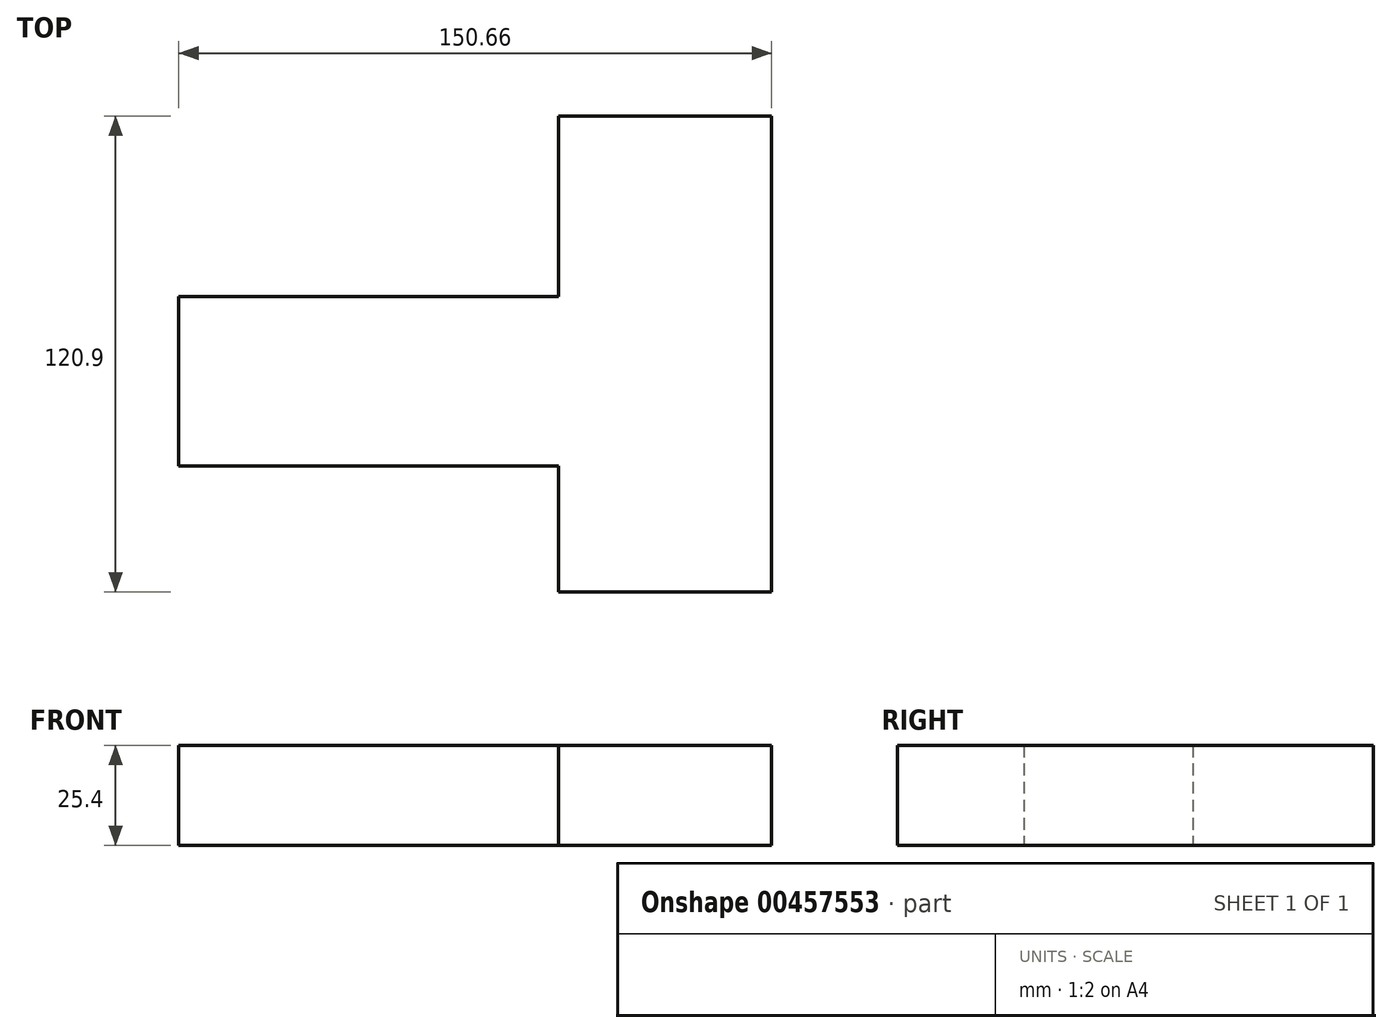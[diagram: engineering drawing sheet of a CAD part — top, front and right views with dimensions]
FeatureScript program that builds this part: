
annotation { "Feature Type Name" : "Feature", "Feature Type Description" : "" }
export const myFeature = defineFeature(function(context is Context, id is Id, definition is map)
    precondition{}
    {
        {
            var Q0;
            Q0=qCreatedBy(makeId("Top.planeOp"),FACE);
            var sketch = newSketch(context, id + "F0", { "sketchPlane" : qUnion([Q0])});
            skLineSegment(sketch, "E0.bottom", {"start": v(0, 21.5) * mm, "end": v(-96.48, 21.5) * mm});
            skLineSegment(sketch, "E0.top", {"start": v(0, -21.5) * mm, "end": v(-96.48, -21.5) * mm});
            skLineSegment(sketch, "E0.left", {"start": v(0, 21.5) * mm, "end": v(0, -21.5) * mm});
            skLineSegment(sketch, "E0.right", {"start": v(-96.48, 21.5) * mm, "end": v(-96.48, -21.5) * mm});
            skPoint(sketch, "E0.middle", {"position": v(-48.24, 0) * mm});
            skLineSegment(sketch, "E1.bottom", {"start": v(0, 67.35) * mm, "end": v(54.18, 67.35) * mm});
            skLineSegment(sketch, "E1.top", {"start": v(0, -53.55) * mm, "end": v(54.18, -53.55) * mm});
            skLineSegment(sketch, "E1.left", {"start": v(0, 67.35) * mm, "end": v(0, -53.55) * mm});
            skLineSegment(sketch, "E1.right", {"start": v(54.18, 67.35) * mm, "end": v(54.18, -53.55) * mm});
            skPoint(sketch, "E1.middle", {"position": v(27.1, 6.9) * mm});
            skSolve(sketch);
        }
        {
            var Q0;
            {var subQ0=sQuery(id+"F0.wireOp",EDGE,"E0.bottom");Q0=makeQuery(id+"F0.imprint","IMPRINT",FACE,{"disambiguationData":[TD([[makeQuery(id+"F0.imprint","IMPRINT",EDGE,{"derivedFrom":subQ0}),1.0]])]});}
            var Q1;
            {var subQ3=sQuery(id+"F0.wireOp",EDGE,"E1.bottom");Q1=makeQuery(id+"F0.imprint","IMPRINT",FACE,{"disambiguationData":[TD([[makeQuery(id+"F0.imprint","IMPRINT",EDGE,{"derivedFrom":subQ3}),-1.0]])]});}
            extrude(context, id + "F1", {"entities" : qUnion([Q0, Q1]), "depth" : 25.4 * mm});
        }
    });
